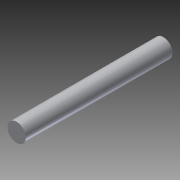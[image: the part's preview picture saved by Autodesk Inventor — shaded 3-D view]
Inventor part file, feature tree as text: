
AUTODESK INVENTOR PART (.ipt)
format: ipt  version: 2013 (Build 170138000, 138)  size: 69,632 bytes
history: native  units: in
note: dims shown in document units (in); Inventor stores cm internally (conversion verified against a paired STEP export)
features: extrude x1, sketch x1
ambient origin geometry x8: Origin, YZ Plane, XZ Plane, XY Plane, X Axis, Y Axis, Z Axis, Center Point
bodies: Solid1 (feature_tree)
feature tree (2):
  extrude  "Extrusion1"  Depth=1.5in TaperAngle=0.0deg
  sketch  "Sketch1"  dims[d0=0.1875in d1=1.5in d2=0.0in]
